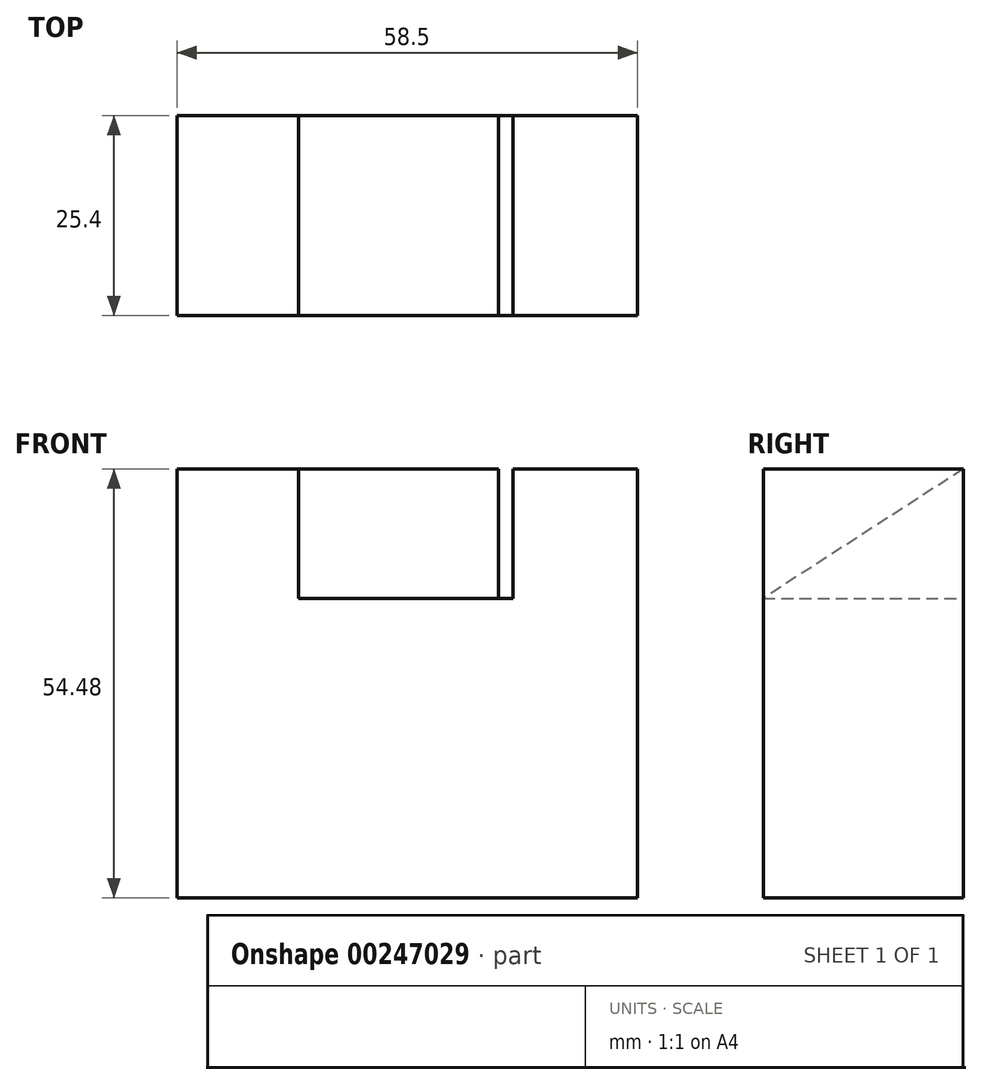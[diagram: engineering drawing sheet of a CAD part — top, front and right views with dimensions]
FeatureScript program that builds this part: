
annotation { "Feature Type Name" : "Feature", "Feature Type Description" : "" }
export const myFeature = defineFeature(function(context is Context, id is Id, definition is map)
    precondition{}
    {
        {
            var Q0;
            Q0=qCreatedBy(makeId("Front.planeOp"),FACE);
            var sketch = newSketch(context, id + "F0", { "sketchPlane" : qUnion([Q0])});
            skLineSegment(sketch, "E0", {"start": v(-24.14, -48.44) * mm, "end": v(34.36, -48.44) * mm});
            skLineSegment(sketch, "E1", {"start": v(34.36, -48.44) * mm, "end": v(34.36, 6.04) * mm});
            skPoint(sketch, "E2.start.orphan", {"position": v(-36.21, -48.44) * mm});
            skPoint(sketch, "E3.end.orphan", {"position": v(-36.21, 6.04) * mm});
            skPoint(sketch, "E4.end.orphan", {"position": v(-9.9, 6.04) * mm});
            skLineSegment(sketch, "E5", {"start": v(34.36, 6.04) * mm, "end": v(18.57, 6.04) * mm});
            skLineSegment(sketch, "E6", {"start": v(18.57, 6.04) * mm, "end": v(18.57, -10.37) * mm});
            skLineSegment(sketch, "E7", {"start": v(18.57, -10.37) * mm, "end": v(-8.67, -10.37) * mm});
            skLineSegment(sketch, "E8", {"start": v(-8.67, -10.37) * mm, "end": v(-8.67, 6.04) * mm});
            skLineSegment(sketch, "E9", {"start": v(-8.67, 6.04) * mm, "end": v(-24.14, 6.04) * mm});
            skLineSegment(sketch, "E10", {"start": v(-24.14, 6.04) * mm, "end": v(-24.14, -48.44) * mm});
            skPoint(sketch, "E11.orphan", {"position": v(-31.57, -48.44) * mm});
            skSolve(sketch);
        }
        {
            var Q0;
            Q0=makeQuery(id+"F0.imprint","IMPRINT",FACE,{"disambiguationData":[TD([[makeQuery(id+"F0.imprint","IMPRINT",EDGE,{"derivedFrom":sQuery(id+"F0.wireOp",EDGE,"E0")}),1.0]])]});
            extrude(context, id + "F1", {"entities" : qUnion([Q0]), "depth" : 25.4 * mm});
        }
        {
            var Q0;
            Q0=makeQuery(id+"F1.opExtrude","SWEPT_FACE",FACE,{"disambiguationData":[OSD([sQuery(id+"F0.wireOp",EDGE,"E8")])]});
            var sketch = newSketch(context, id + "F2", { "sketchPlane" : qUnion([Q0])});
            skLineSegment(sketch, "E12", {"start": v(-25.4, -10.37) * mm, "end": v(0, -10.37) * mm});
            skLineSegment(sketch, "E13", {"start": v(0, -10.37) * mm, "end": v(0, 6.04) * mm});
            skLineSegment(sketch, "E14", {"start": v(0, 6.04) * mm, "end": v(-25.4, -10.37) * mm});
            skSolve(sketch);
        }
        {
            var Q0;
            Q0 = qSketchRegion(id + "F2", true);
            extrude(context, id + "F3", {"entities" : qUnion([Q0]), "operationType" : NewBodyOperationType.ADD, "depth" : 25.4 * mm});
        }
    });
